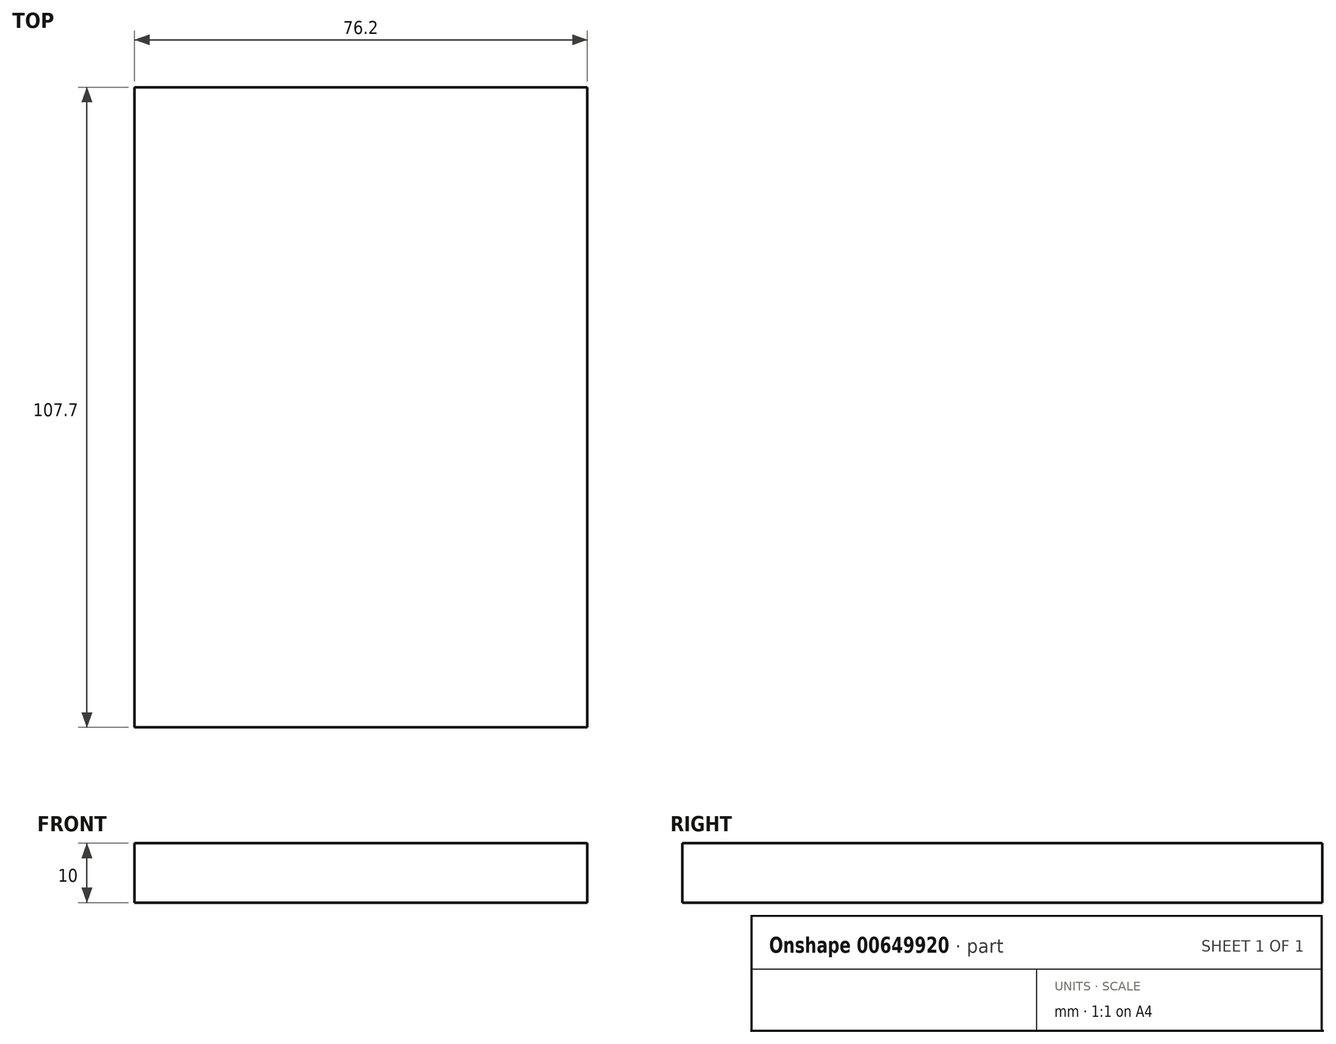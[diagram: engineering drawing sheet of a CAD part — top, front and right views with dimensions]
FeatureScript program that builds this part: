
annotation { "Feature Type Name" : "Feature", "Feature Type Description" : "" }
export const myFeature = defineFeature(function(context is Context, id is Id, definition is map)
    precondition{}
    {
        {
            var Q0;
            Q0=qCreatedBy(makeId("Front.planeOp"),FACE);
            var sketch = newSketch(context, id + "F0", { "sketchPlane" : qUnion([Q0])});
            skLineSegment(sketch, "E0.bottom", {"start": v(-38.1, 17.58) * mm, "end": v(38.1, 17.58) * mm});
            skLineSegment(sketch, "E0.top", {"start": v(-38.1, 7.58) * mm, "end": v(38.1, 7.58) * mm});
            skLineSegment(sketch, "E0.left", {"start": v(-38.1, 17.58) * mm, "end": v(-38.1, 7.58) * mm});
            skLineSegment(sketch, "E0.right", {"start": v(38.1, 17.58) * mm, "end": v(38.1, 7.58) * mm});
            skSolve(sketch);
        }
        {
            var Q0;
            Q0=makeQuery(id+"F0.imprint","IMPRINT",FACE,{"disambiguationData":[TD([[makeQuery(id+"F0.imprint","IMPRINT",EDGE,{"derivedFrom":sQuery(id+"F0.wireOp",EDGE,"E0.bottom")}),-1.0]])]});
            extrude(context, id + "F1", {"entities" : qUnion([Q0]), "depth" : 68.33 * mm, "offsetDistance" : 25.4 * mm, "hasSecondDirection" : true, "secondDirectionOppositeDirection" : true, "secondDirectionDepth" : 39.37 * mm});
        }
    });
